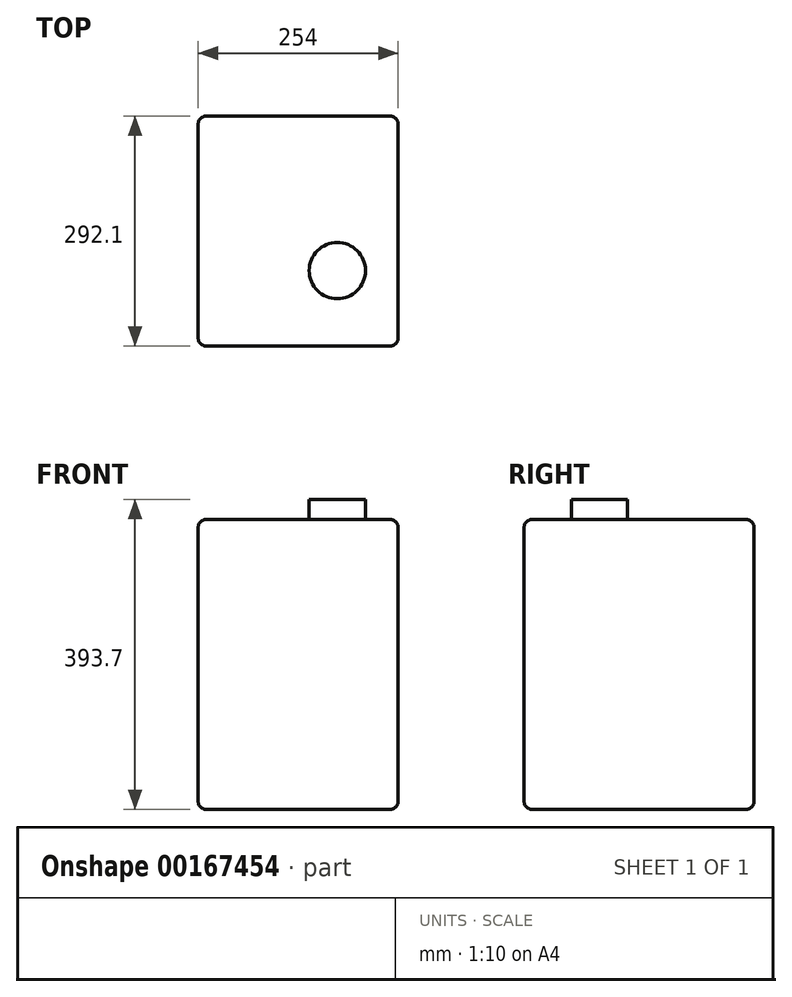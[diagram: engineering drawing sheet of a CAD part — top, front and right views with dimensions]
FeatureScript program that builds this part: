
annotation { "Feature Type Name" : "Feature", "Feature Type Description" : "" }
export const myFeature = defineFeature(function(context is Context, id is Id, definition is map)
    precondition{}
    {
        {
            var Q0;
            Q0=qCreatedBy(makeId("Front.planeOp"),FACE);
            var sketch = newSketch(context, id + "F0", { "sketchPlane" : qUnion([Q0])});
            skLineSegment(sketch, "E0.bottom", {"start": v(-126.7, 155.45) * mm, "end": v(127.3, 155.45) * mm});
            skLineSegment(sketch, "E0.top", {"start": v(-126.7, -212.85) * mm, "end": v(127.3, -212.85) * mm});
            skLineSegment(sketch, "E0.left", {"start": v(-126.7, 155.45) * mm, "end": v(-126.7, -212.85) * mm});
            skLineSegment(sketch, "E0.right", {"start": v(127.3, 155.45) * mm, "end": v(127.3, -212.85) * mm});
            skSolve(sketch);
        }
        {
            var Q0;
            Q0 = qSketchRegion(id + "F0", true);
            extrude(context, id + "F1", {"entities" : qUnion([Q0]), "depth" : 292.1 * mm});
        }
        {
            var Q0;
            Q0=makeQuery(id+"F1.opExtrude","SWEPT_FACE",FACE,{"disambiguationData":[OSD([sQuery(id+"F0.wireOp",EDGE,"E0.bottom")])]});
            var sketch = newSketch(context, id + "F2", { "sketchPlane" : qUnion([Q0])});
            skCircle(sketch, "E1", {"center": v(50.06, -196.3) * mm, "radius": 35.73 * mm});
            skSolve(sketch);
        }
        {
            var Q0;
            Q0=makeQuery(id+"F2.imprint","IMPRINT",FACE,{"disambiguationData":[TD([[makeQuery(id+"F2.imprint","IMPRINT",EDGE,{"derivedFrom":sQuery(id+"F2.wireOp",EDGE,"E1")}),1.0]])]});
            var Q1;
            Q1=sQuery(id+"F2.wireOp",EDGE,"E1");
            extrude(context, id + "F3", {"entities" : qUnion([Q0]), "operationType" : NewBodyOperationType.ADD, "surfaceEntities" : qUnion([Q1]), "depth" : 25.4 * mm});
        }
        {
            var Q0;
            Q0=makeQuery(id+"F1.opExtrude","CAP_EDGE",EDGE,{"disambiguationData":[OSD([sQuery(id+"F0.wireOp",EDGE,"E0.left")])],"isStart":false});
            var Q1;
            Q1=makeQuery(id+"F1.opExtrude","CAP_EDGE",EDGE,{"disambiguationData":[OSD([sQuery(id+"F0.wireOp",EDGE,"E0.bottom")])],"isStart":false});
            var Q2;
            Q2=makeQuery(id+"F1.opExtrude","SWEPT_EDGE",EDGE,{"disambiguationData":[OSD([sQuery(id+"F0.wireOp",EDGE,"E0.bottom"),sQuery(id+"F0.wireOp",EDGE,"E0.left")])]});
            var Q3;
            Q3=makeQuery(id+"F1.opExtrude","CAP_EDGE",EDGE,{"disambiguationData":[OSD([sQuery(id+"F0.wireOp",EDGE,"E0.bottom")])],"isStart":true});
            var Q4;
            Q4=makeQuery(id+"F1.opExtrude","SWEPT_EDGE",EDGE,{"disambiguationData":[OSD([sQuery(id+"F0.wireOp",EDGE,"E0.bottom"),sQuery(id+"F0.wireOp",EDGE,"E0.right")])]});
            var Q5;
            Q5=makeQuery(id+"F1.opExtrude","CAP_EDGE",EDGE,{"disambiguationData":[OSD([sQuery(id+"F0.wireOp",EDGE,"E0.left")])],"isStart":true});
            var Q6;
            Q6=makeQuery(id+"F1.opExtrude","SWEPT_EDGE",EDGE,{"disambiguationData":[OSD([sQuery(id+"F0.wireOp",EDGE,"E0.top"),sQuery(id+"F0.wireOp",EDGE,"E0.left")])]});
            var Q7;
            Q7=makeQuery(id+"F1.opExtrude","CAP_EDGE",EDGE,{"disambiguationData":[OSD([sQuery(id+"F0.wireOp",EDGE,"E0.top")])],"isStart":true});
            var Q8;
            Q8=makeQuery(id+"F1.opExtrude","CAP_EDGE",EDGE,{"disambiguationData":[OSD([sQuery(id+"F0.wireOp",EDGE,"E0.right")])],"isStart":true});
            var Q9;
            Q9=makeQuery(id+"F1.opExtrude","CAP_EDGE",EDGE,{"disambiguationData":[OSD([sQuery(id+"F0.wireOp",EDGE,"E0.right")])],"isStart":false});
            var Q10;
            Q10=makeQuery(id+"F1.opExtrude","CAP_EDGE",EDGE,{"disambiguationData":[OSD([sQuery(id+"F0.wireOp",EDGE,"E0.top")])],"isStart":false});
            var Q11;
            Q11=makeQuery(id+"F1.opExtrude","SWEPT_EDGE",EDGE,{"disambiguationData":[OSD([sQuery(id+"F0.wireOp",EDGE,"E0.top"),sQuery(id+"F0.wireOp",EDGE,"E0.right")])]});
            fillet(context, id + "F4", {"entities" : qUnion([Q0, Q1, Q2, Q3, Q4, Q5, Q6, Q7, Q8, Q9, Q10, Q11]), "radius" : 10.16 * mm, "tangentPropagation" : true, "allowEdgeOverflow" : false});
        }
    });
